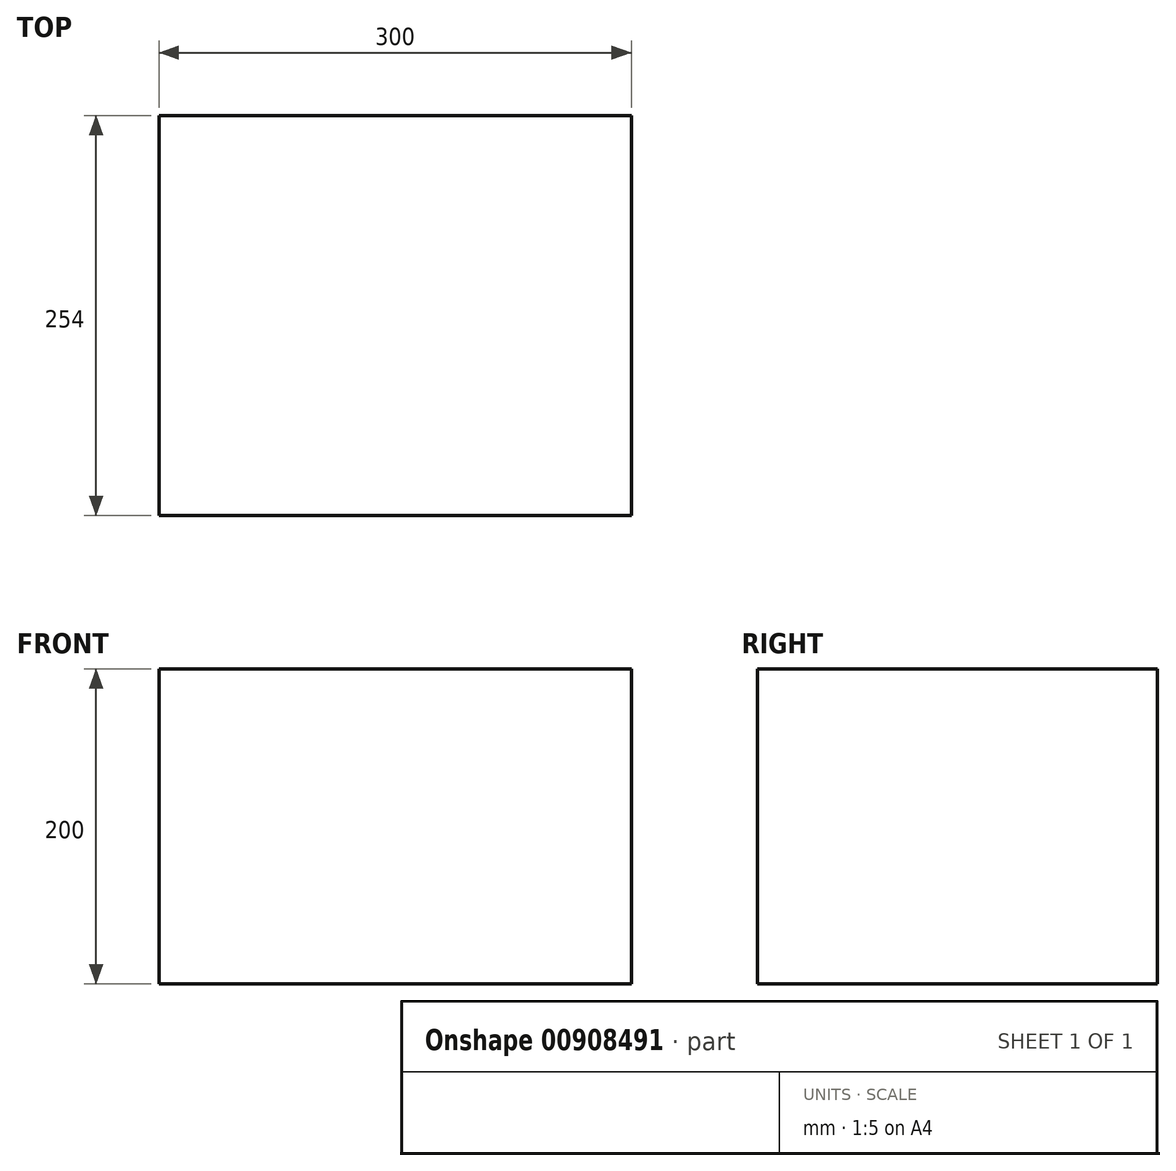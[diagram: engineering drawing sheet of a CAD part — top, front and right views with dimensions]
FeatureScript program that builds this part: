
annotation { "Feature Type Name" : "Feature", "Feature Type Description" : "" }
export const myFeature = defineFeature(function(context is Context, id is Id, definition is map)
    precondition{}
    {
        {
            var Q0;
            Q0=qCreatedBy(makeId("Front.planeOp"),FACE);
            var sketch = newSketch(context, id + "F0", { "sketchPlane" : qUnion([Q0])});
            skLineSegment(sketch, "E0.bottom", {"start": v(-3337.8, -2332.03) * mm, "end": v(-3037.8, -2332.03) * mm});
            skLineSegment(sketch, "E0.top", {"start": v(-3337.8, -2532.03) * mm, "end": v(-3037.8, -2532.03) * mm});
            skLineSegment(sketch, "E0.left", {"start": v(-3337.8, -2332.03) * mm, "end": v(-3337.8, -2532.03) * mm});
            skLineSegment(sketch, "E0.right", {"start": v(-3037.8, -2332.03) * mm, "end": v(-3037.8, -2532.03) * mm});
            skLineSegment(sketch, "E1", {"start": v(-3266.16, -2532.03) * mm, "end": v(-3266.16, -2913.03) * mm});
            skSolve(sketch);
        }
        {
            var Q0;
            Q0=makeQuery(id+"F0.imprint","IMPRINT",FACE,{"disambiguationData":[TD([[makeQuery(id+"F0.imprint","IMPRINT",EDGE,{"derivedFrom":sQuery(id+"F0.wireOp",EDGE,"E0.bottom")}),-1.0]])]});
            extrude(context, id + "F1", {"entities" : qUnion([Q0]), "depth" : 254 * mm, "offsetDistance" : 25.4 * mm});
        }
    });
